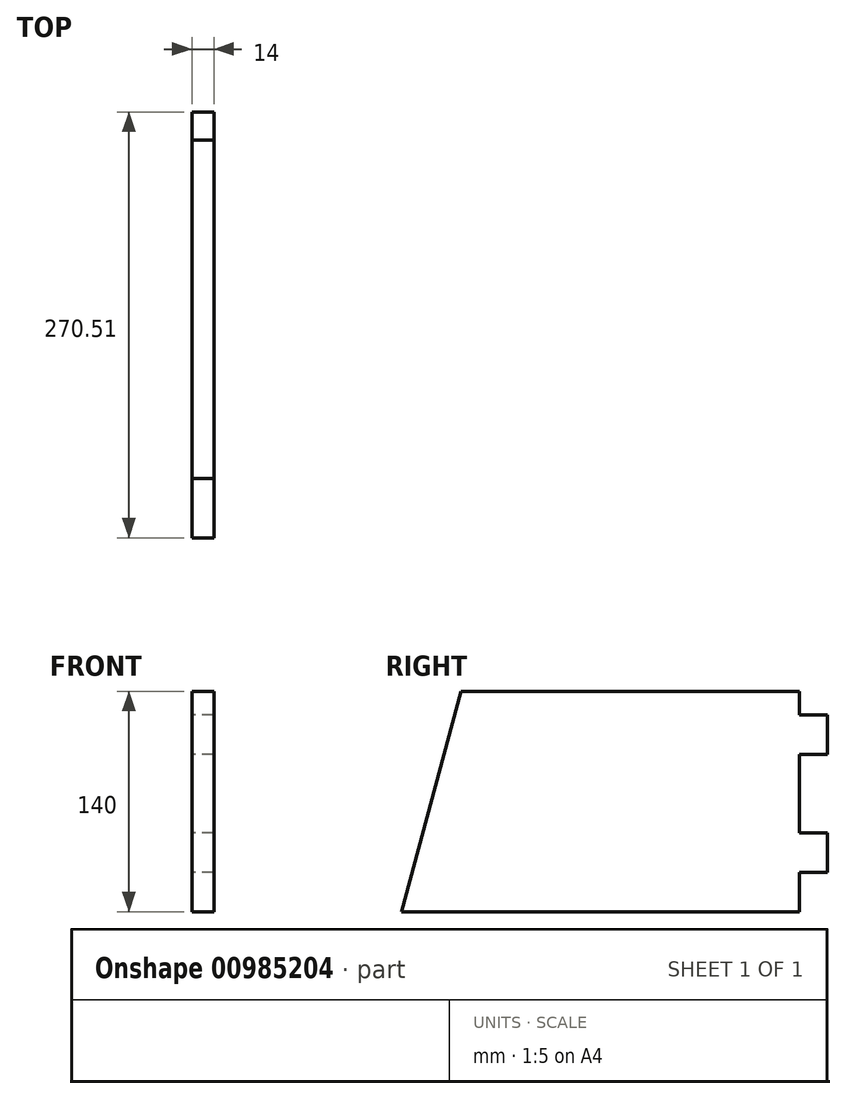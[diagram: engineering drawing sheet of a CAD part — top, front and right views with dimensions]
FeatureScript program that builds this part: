
annotation { "Feature Type Name" : "Feature", "Feature Type Description" : "" }
export const myFeature = defineFeature(function(context is Context, id is Id, definition is map)
    precondition{}
    {
        {
            var Q0;
            Q0=qCreatedBy(makeId("Right.planeOp"),FACE);
            var sketch = newSketch(context, id + "F0", { "sketchPlane" : qUnion([Q0])});
            skLineSegment(sketch, "E0", {"start": v(0, 0) * mm, "end": v(0, 140) * mm});
            skLineSegment(sketch, "E1", {"start": v(0, 140) * mm, "end": v(-215, 140) * mm});
            skLineSegment(sketch, "E2", {"start": v(-215, 140) * mm, "end": v(-252.51, 0) * mm});
            skLineSegment(sketch, "E3", {"start": v(-252.51, 0) * mm, "end": v(0, 0) * mm});
            skLineSegment(sketch, "E4.bottom", {"start": v(0, 25) * mm, "end": v(18, 25) * mm});
            skLineSegment(sketch, "E4.top", {"start": v(0, 50) * mm, "end": v(18, 50) * mm});
            skLineSegment(sketch, "E4.left", {"start": v(0, 25) * mm, "end": v(0, 50) * mm});
            skLineSegment(sketch, "E4.right", {"start": v(18, 25) * mm, "end": v(18, 50) * mm});
            skLineSegment(sketch, "E5.bottom", {"start": v(0, 125) * mm, "end": v(18, 125) * mm});
            skLineSegment(sketch, "E5.top", {"start": v(0, 100) * mm, "end": v(18, 100) * mm});
            skLineSegment(sketch, "E5.left", {"start": v(0, 125) * mm, "end": v(0, 100) * mm});
            skLineSegment(sketch, "E5.right", {"start": v(18, 125) * mm, "end": v(18, 100) * mm});
            skSolve(sketch);
        }
        {
            var Q0;
            {var subQ0=sQuery(id+"F0.wireOp",EDGE,"E5.bottom");var subQ7=sQuery(id+"F0.wireOp",EDGE,"E4.bottom");var subQ12=sQuery(id+"F0.wireOp",EDGE,"E1");Q0=qUnion([makeQuery(id+"F0.imprint","IMPRINT",FACE,{"disambiguationData":[TD([[makeQuery(id+"F0.imprint","IMPRINT",EDGE,{"derivedFrom":subQ7}),1.0]])]}),makeQuery(id+"F0.imprint","IMPRINT",FACE,{"disambiguationData":[TD([[makeQuery(id+"F0.imprint","IMPRINT",EDGE,{"derivedFrom":subQ0}),-1.0]])]}),makeQuery(id+"F0.imprint","IMPRINT",FACE,{"disambiguationData":[TD([[makeQuery(id+"F0.imprint","IMPRINT",EDGE,{"derivedFrom":subQ12}),1.0]])]})]);}
            extrude(context, id + "F1", {"entities" : qUnion([Q0]), "depth" : 14 * mm, "offsetDistance" : 25 * mm});
        }
    });
